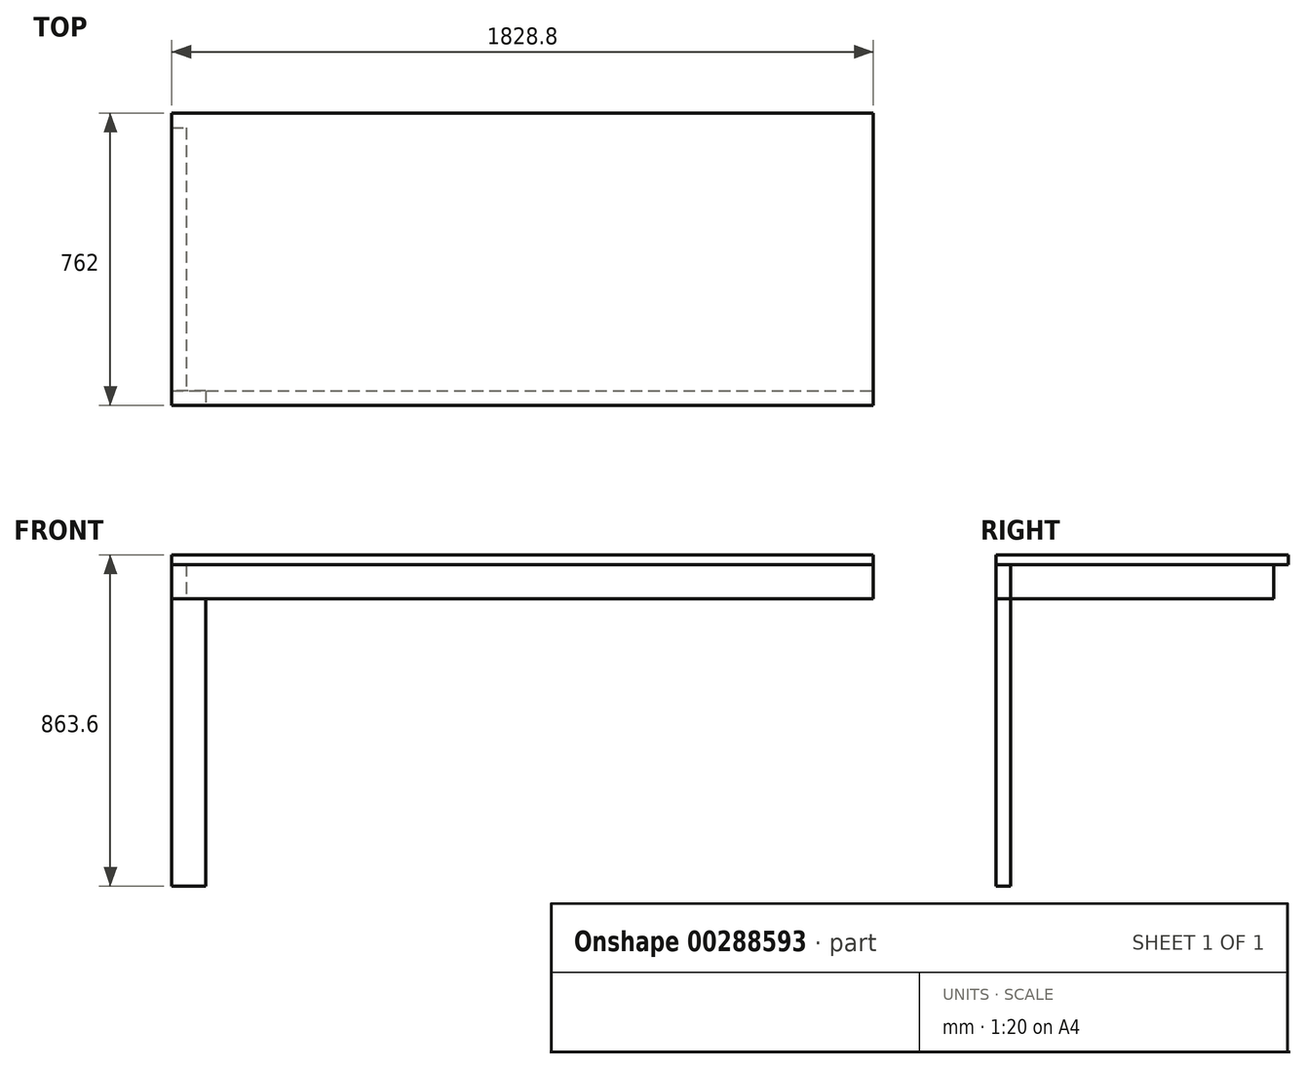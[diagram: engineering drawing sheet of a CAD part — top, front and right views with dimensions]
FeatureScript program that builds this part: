
annotation { "Feature Type Name" : "Feature", "Feature Type Description" : "" }
export const myFeature = defineFeature(function(context is Context, id is Id, definition is map)
    precondition{}
    {
        {
            var Q0;
            Q0=qCreatedBy(makeId("Front.planeOp"),FACE);
            var sketch = newSketch(context, id + "F0", { "sketchPlane" : qUnion([Q0])});
            skLineSegment(sketch, "E0", {"start": v(0, 0) * mm, "end": v(-914.4, 0) * mm});
            skLineSegment(sketch, "E1", {"start": v(-914.4, 0) * mm, "end": v(-914.4, -863.6) * mm});
            skLineSegment(sketch, "E2", {"start": v(-914.4, -863.6) * mm, "end": v(-825.5, -863.6) * mm});
            skLineSegment(sketch, "E3", {"start": v(-825.5, -863.6) * mm, "end": v(-825.5, -25.4) * mm});
            skLineSegment(sketch, "E4", {"start": v(-914.4, -25.4) * mm, "end": v(0, -25.4) * mm});
            skLineSegment(sketch, "E5.MirrorCS", {"start": v(0, 0) * mm, "end": v(914.4, 0) * mm});
            skLineSegment(sketch, "E6.MirrorCS", {"start": v(914.4, -25.4) * mm, "end": v(0, -25.4) * mm});
            skLineSegment(sketch, "E7.MirrorCS", {"start": v(825.5, -863.6) * mm, "end": v(825.5, -25.4) * mm});
            skLineSegment(sketch, "E8.MirrorCS", {"start": v(914.4, 0) * mm, "end": v(914.4, -863.6) * mm});
            skLineSegment(sketch, "E9.MirrorCS", {"start": v(914.4, -863.6) * mm, "end": v(825.5, -863.6) * mm});
            skLineSegment(sketch, "E10", {"start": v(0, -114.3) * mm, "end": v(-914.4, -114.3) * mm});
            skLineSegment(sketch, "E11.MirrorCS", {"start": v(0, -114.3) * mm, "end": v(914.4, -114.3) * mm});
            skLineSegment(sketch, "E12", {"start": v(-876.3, -25.4) * mm, "end": v(-876.3, -114.3) * mm});
            skLineSegment(sketch, "E13.MirrorCS", {"start": v(876.3, -25.4) * mm, "end": v(876.3, -114.3) * mm});
            skPoint(sketch, "E14.orphan", {"position": v(-876.3, 0) * mm});
            skPoint(sketch, "E15.orphan", {"position": v(-825.5, 0) * mm});
            skPoint(sketch, "E16.orphan", {"position": v(-876.3, -863.6) * mm});
            skPoint(sketch, "E17.orphan", {"position": v(876.3, 0) * mm});
            skPoint(sketch, "E18.orphan", {"position": v(876.3, -863.6) * mm});
            skPoint(sketch, "E19.orphan", {"position": v(825.5, 0) * mm});
            skSolve(sketch);
        }
        {
            var Q0;
            {var subQ5=sQuery(id+"F0.wireOp",EDGE,"E0");Q0=makeQuery(id+"F0.imprint","IMPRINT",FACE,{"disambiguationData":[TD([[makeQuery(id+"F0.imprint","IMPRINT",EDGE,{"derivedFrom":subQ5}),1.0]])]});}
            extrude(context, id + "F1", {"entities" : qUnion([Q0]), "oppositeDirection" : true, "depth" : 762 * mm});
        }
        {
            var Q0;
            {var subQ4=sQuery(id+"F0.wireOp",EDGE,"E2");Q0=makeQuery(id+"F0.imprint","IMPRINT",FACE,{"disambiguationData":[TD([[makeQuery(id+"F0.imprint","IMPRINT",EDGE,{"derivedFrom":subQ4}),1.0]])]});}
            extrude(context, id + "F2", {"entities" : qUnion([Q0]), "oppositeDirection" : true, "depth" : 38.1 * mm});
        }
        {
            var Q0;
            {var subQ5=sQuery(id+"F0.wireOp",EDGE,"E12");Q0=makeQuery(id+"F0.imprint","IMPRINT",FACE,{"disambiguationData":[TD([[makeQuery(id+"F0.imprint","IMPRINT",EDGE,{"derivedFrom":subQ5}),-1.0]])]});}
            extrude(context, id + "F3", {"entities" : qUnion([Q0]), "oppositeDirection" : true, "depth" : 685.8 * mm});
        }
        {
            var Q0;
            Q0=makeQuery(id+"F3.opExtrude","SWEPT_BODY",BODY,{"disambiguationData":[OSD([sQuery(id+"F0.wireOp",EDGE,"E1"),sQuery(id+"F0.wireOp",EDGE,"E4"),sQuery(id+"F0.wireOp",EDGE,"E10"),sQuery(id+"F0.wireOp",EDGE,"E12")])]});
            var Q1;
            Q1=makeQuery(id+"F3.opExtrude","SWEPT_EDGE",EDGE,{"disambiguationData":[OSD([sQuery(id+"F0.wireOp",EDGE,"E1"),sQuery(id+"F0.wireOp",EDGE,"E4")])]});
            var Q2;
            Q2=makeQuery(id+"F3.opExtrude","SWEPT_EDGE",EDGE,{"disambiguationData":[OSD([sQuery(id+"F0.wireOp",EDGE,"E1"),sQuery(id+"F0.wireOp",EDGE,"E4")])]});
            transform(context, id + "F4", {"entities" : qUnion([Q0]), "transformType" : TransformType.TRANSLATION_DISTANCE, "transformDirection" : qUnion([Q2]), "distance" : 38.1 * mm, "oppositeDirection" : true, "makeCopy" : false});
        }
        {
            var Q0;
            {var subQ5=sQuery(id+"F0.wireOp",EDGE,"E4");var subQ7=sQuery(id+"F0.wireOp",EDGE,"E3");var subQ8=makeQuery(id+"F0.imprint","INTERSECT",VERTEX,{"derivedFrom":[subQ7,subQ5]});Q0=makeQuery(id+"F0.imprint","IMPRINT",FACE,{"disambiguationData":[TD([[makeQuery(id+"F0.imprint","IMPRINT",EDGE,{"disambiguationData":[TD([[subQ8,1.0]])],"derivedFrom":subQ7}),-1.0]])]});}
            var Q1;
            {var subQ5=sQuery(id+"F0.wireOp",EDGE,"E12");Q1=makeQuery(id+"F0.imprint","IMPRINT",FACE,{"disambiguationData":[TD([[makeQuery(id+"F0.imprint","IMPRINT",EDGE,{"derivedFrom":subQ5}),1.0]])]});}
            var Q2;
            {var subQ5=sQuery(id+"F0.wireOp",EDGE,"E12");Q2=makeQuery(id+"F0.imprint","IMPRINT",FACE,{"disambiguationData":[TD([[makeQuery(id+"F0.imprint","IMPRINT",EDGE,{"derivedFrom":subQ5}),-1.0]])]});}
            var Q3;
            {var subQ3=sQuery(id+"F0.wireOp",EDGE,"E13.MirrorCS");Q3=makeQuery(id+"F0.imprint","IMPRINT",FACE,{"disambiguationData":[TD([[makeQuery(id+"F0.imprint","IMPRINT",EDGE,{"derivedFrom":subQ3}),-1.0]])]});}
            var Q4;
            {var subQ3=sQuery(id+"F0.wireOp",EDGE,"E13.MirrorCS");Q4=makeQuery(id+"F0.imprint","IMPRINT",FACE,{"disambiguationData":[TD([[makeQuery(id+"F0.imprint","IMPRINT",EDGE,{"derivedFrom":subQ3}),1.0]])]});}
            extrude(context, id + "F5", {"entities" : qUnion([Q0, Q1, Q2, Q3, Q4]), "oppositeDirection" : true, "depth" : 38.1 * mm});
        }
    });
